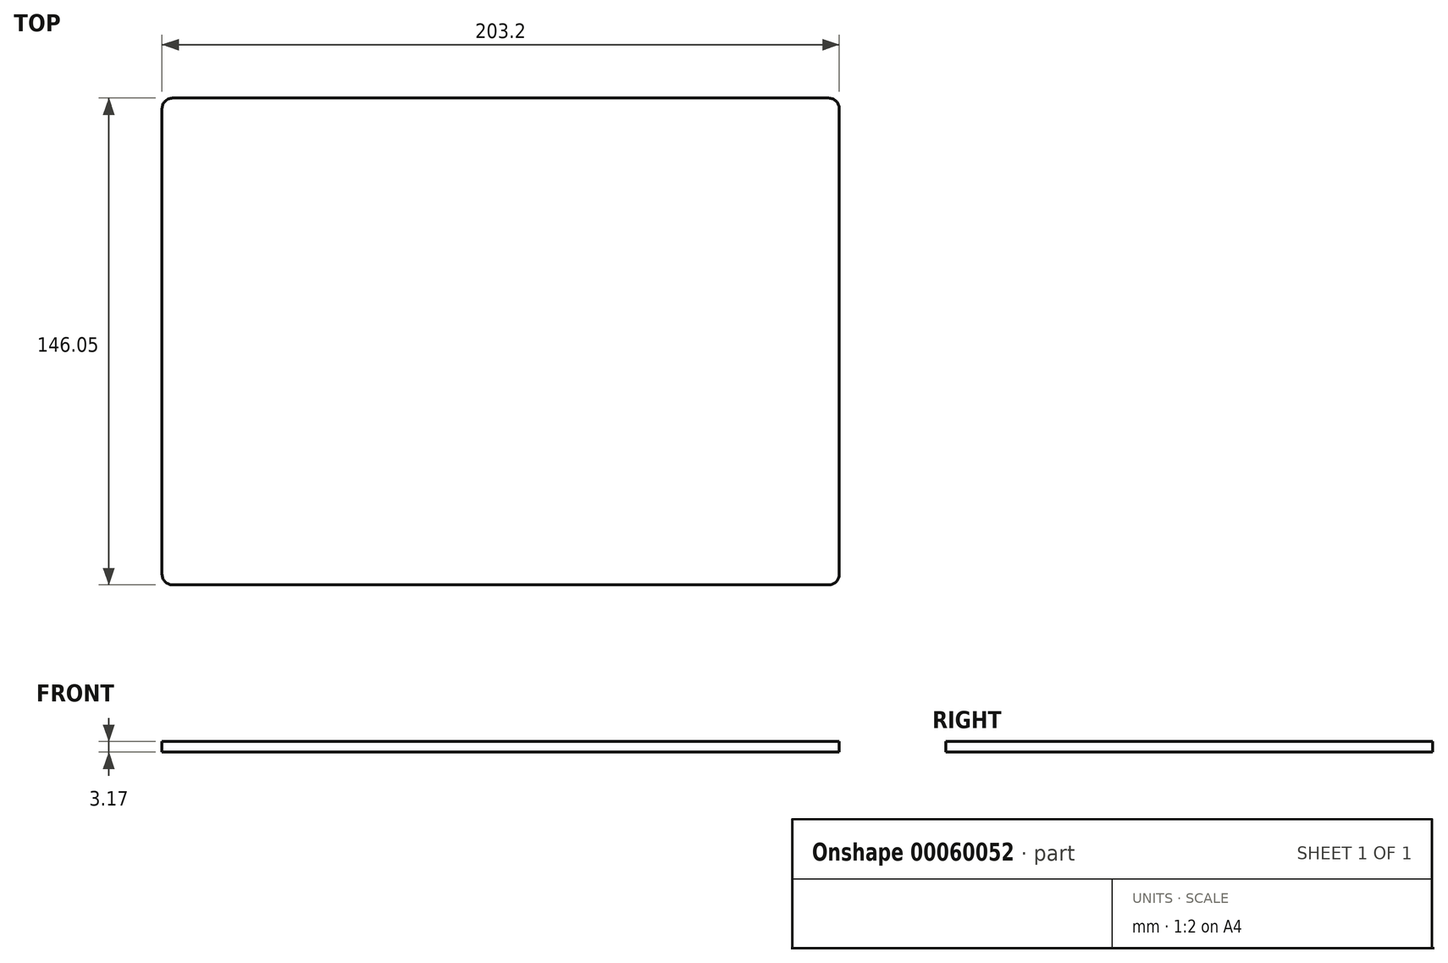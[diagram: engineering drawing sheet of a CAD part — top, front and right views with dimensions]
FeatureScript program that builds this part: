
annotation { "Feature Type Name" : "Feature", "Feature Type Description" : "" }
export const myFeature = defineFeature(function(context is Context, id is Id, definition is map)
    precondition{}
    {
        {
            var Q0;
            Q0=qCreatedBy(makeId("Top.planeOp"),FACE);
            var sketch = newSketch(context, id + "F0", { "sketchPlane" : qUnion([Q0])});
            skLineSegment(sketch, "E0.bottom", {"start": v(3.17, 0) * mm, "end": v(200.03, 0) * mm});
            skLineSegment(sketch, "E0.top", {"start": v(3.17, 146.05) * mm, "end": v(200.03, 146.05) * mm});
            skLineSegment(sketch, "E0.left", {"start": v(0, 3.17) * mm, "end": v(0, 142.88) * mm});
            skLineSegment(sketch, "E0.right", {"start": v(203.2, 3.17) * mm, "end": v(203.2, 142.88) * mm});
            skPoint(sketch, "E1.visualSharp", {"position": v(0, 146.05) * mm});
            skArc(sketch, "E1.filletArc", {"start": v(3.17, 146.05) * mm, "mid": v(0.93, 145.12) * mm, "end": v(0, 142.88) * mm});
            skPoint(sketch, "E2.visualSharp", {"position": v(203.2, 146.05) * mm});
            skArc(sketch, "E2.filletArc", {"start": v(203.2, 142.88) * mm, "mid": v(202.27, 145.12) * mm, "end": v(200.03, 146.05) * mm});
            skPoint(sketch, "E3.visualSharp", {"position": v(203.2, 0) * mm});
            skArc(sketch, "E3.filletArc", {"start": v(200.03, 0) * mm, "mid": v(202.27, 0.93) * mm, "end": v(203.2, 3.18) * mm});
            skPoint(sketch, "E4.visualSharp", {"position": v(0, 0) * mm});
            skArc(sketch, "E4.filletArc", {"start": v(0, 3.17) * mm, "mid": v(0.93, 0.93) * mm, "end": v(3.17, 0) * mm});
            skSolve(sketch);
        }
        {
            var Q0;
            Q0 = qSketchRegion(id + "F0", true);
            extrude(context, id + "F1", {"entities" : qUnion([Q0]), "depth" : 3.17 * mm});
        }
    });
